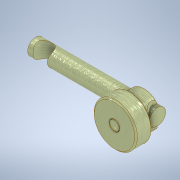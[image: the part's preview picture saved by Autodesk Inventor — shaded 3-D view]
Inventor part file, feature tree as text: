
AUTODESK INVENTOR PART (.ipt)
format: ipt  version: 2021.3 (Build 253353000, 353)  size: 268,288 bytes
history: native  units: mm
features: sketch x9, extrude x8, chamfer x1, fillet x1
ambient origin geometry x8: Origin, YZ Plane, XZ Plane, XY Plane, X Axis, Y Axis, Z Axis, Center Point
bodies: Solid1 (feature_tree)
feature tree (19):
  extrude  "Extrusion1"  Depth=2.0mm TaperAngle=0.0deg
  chamfer  "Chamfer1"  Distance=2.0mm Angle=45.0deg
  extrude  "Extrusion3"  Depth=10.0mm TaperAngle=0.0deg
  extrude  "Extrusion4"  Depth=2.0mm TaperAngle=0.0deg
  fillet  "Fillet1"  Radius=2.0mm
  extrude  "Extrusion5"  Depth=23.0mm TaperAngle=0.0deg
  extrude  "Extrusion6"  Depth=23.0mm TaperAngle=0.0deg
  sketch  "Sketch9"  dims[d24=12.0mm d25=20.0mm d26=0.0mm]
  extrude  "Extrusion7"  Depth=20.0mm TaperAngle=0.0deg
  extrude  "Extrusion8"  Depth=12.0mm
  extrude  "Extrusion13"  Depth=0.5mm
  sketch  "Sketch1"  dims[d0=32.0mm d1=12.0mm d2=0.0mm d3=1.0mm d4=2.0mm d5=45.0deg]
  sketch  "Sketch3"  dims[d10=25.0mm d11=10.0mm d12=0.0mm]
  sketch  "Sketch4"  dims[d13=12.0mm d14=27.0mm d15=0.0mm d16=2.0mm]
  sketch  "Sketch6"  dims[d18=8.0mm d19=23.0mm d20=0.0mm]
  sketch  "Sketch7"  dims[d21=7.0mm d22=23.0mm d23=0.0mm]
  sketch  "Sketch10"  dims[d27=70.0mm d28=0.0mm d39=12.0mm]
  sketch  "Sketch11"  dims[d40=50.0mm d41=0.0mm d7=0.5mm]
  sketch  "Sketch16"  dims[d8=0.872665mm d9=0.5mm d42=0.872665mm]
